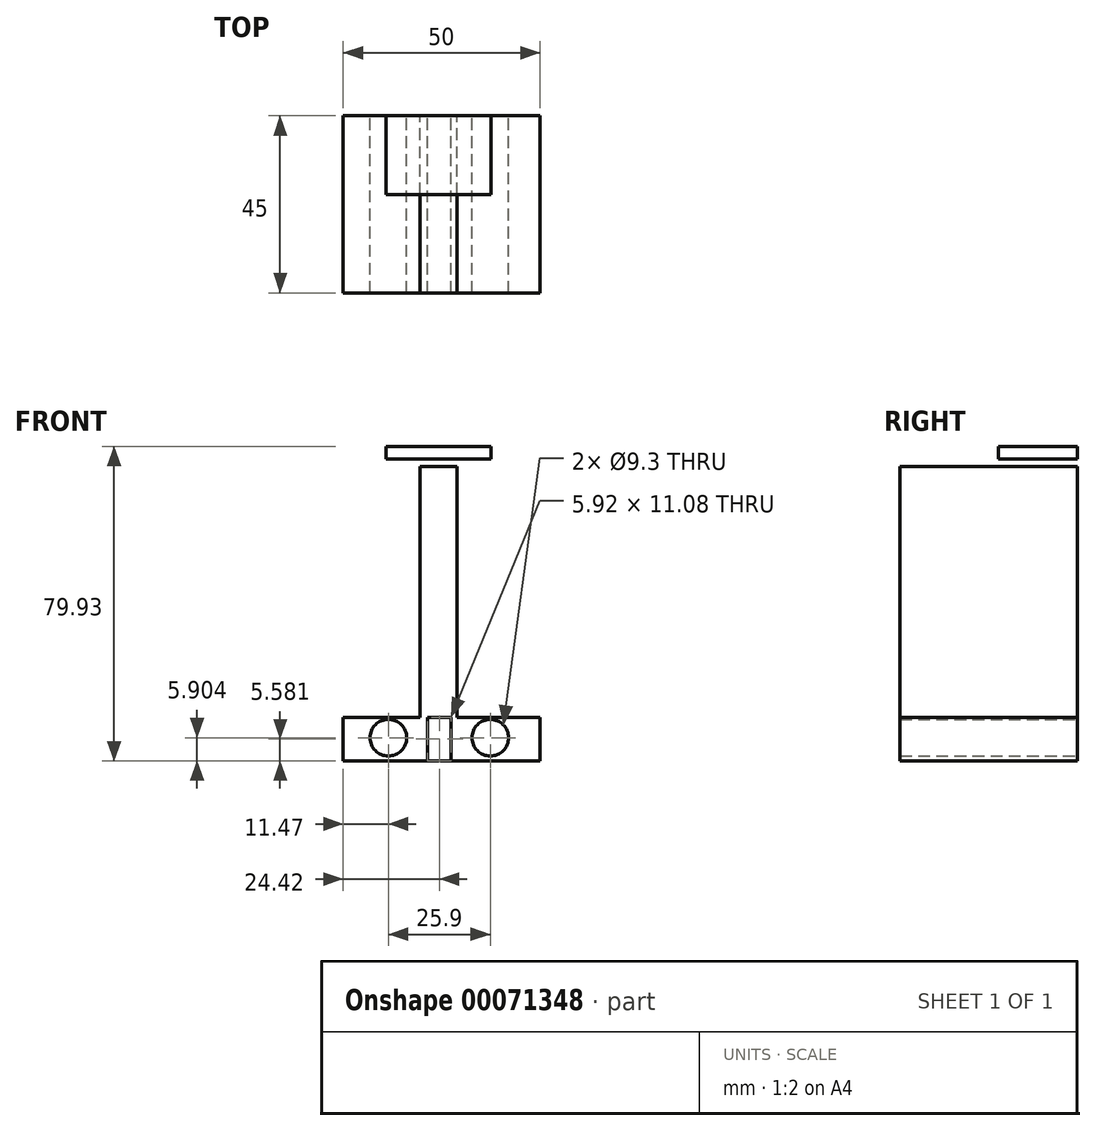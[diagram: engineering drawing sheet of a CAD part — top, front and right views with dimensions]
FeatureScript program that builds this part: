
annotation { "Feature Type Name" : "Feature", "Feature Type Description" : "" }
export const myFeature = defineFeature(function(context is Context, id is Id, definition is map)
    precondition{}
    {
        {
            var Q0;
            Q0=qCreatedBy(makeId("Front.planeOp"),FACE);
            var sketch = newSketch(context, id + "F0", { "sketchPlane" : qUnion([Q0])});
            skLineSegment(sketch, "E0.bottom", {"start": v(-4.86, 63.71) * mm, "end": v(4.48, 63.71) * mm});
            skLineSegment(sketch, "E0.top", {"start": v(-4.86, -11.08) * mm, "end": v(4.48, -11.08) * mm});
            skLineSegment(sketch, "E0.left", {"start": v(-4.86, 63.71) * mm, "end": v(-4.86, -11.08) * mm});
            skLineSegment(sketch, "E0.right", {"start": v(4.48, 63.71) * mm, "end": v(4.48, -11.08) * mm});
            skLineSegment(sketch, "E1.bottom", {"start": v(-24.42, 0) * mm, "end": v(25.58, 0) * mm});
            skLineSegment(sketch, "E1.top", {"start": v(-24.42, -11.12) * mm, "end": v(25.58, -11.12) * mm});
            skLineSegment(sketch, "E1.left", {"start": v(-24.42, 0) * mm, "end": v(-24.42, -11.12) * mm});
            skLineSegment(sketch, "E1.right", {"start": v(25.58, 0) * mm, "end": v(25.58, -11.12) * mm});
            skCircle(sketch, "E2", {"center": v(-12.95, -5.22) * mm, "radius": 4.65 * mm});
            skCircle(sketch, "E3.MirrorC", {"center": v(12.95, -5.22) * mm, "radius": 4.65 * mm});
            skLineSegment(sketch, "E4", {"start": v(-2.96, -11.08) * mm, "end": v(-2.96, 63.71) * mm});
            skLineSegment(sketch, "E5", {"start": v(-2.96, 63.71) * mm, "end": v(2.36, 63.71) * mm});
            skLineSegment(sketch, "E6.MirrorCS", {"start": v(2.96, -11.08) * mm, "end": v(2.96, 63.71) * mm});
            skLineSegment(sketch, "E7", {"start": v(-4.86, 63.71) * mm, "end": v(-6.73, 65.65) * mm});
            skLineSegment(sketch, "E8.MirrorCS", {"start": v(4.86, 63.71) * mm, "end": v(6.73, 65.65) * mm});
            skLineSegment(sketch, "E9.bottom", {"start": v(-13.5, 68.8) * mm, "end": v(13.12, 68.8) * mm});
            skLineSegment(sketch, "E9.top", {"start": v(-13.5, 65.63) * mm, "end": v(13.12, 65.63) * mm});
            skLineSegment(sketch, "E9.left", {"start": v(-13.5, 68.8) * mm, "end": v(-13.5, 65.63) * mm});
            skLineSegment(sketch, "E9.right", {"start": v(13.12, 68.8) * mm, "end": v(13.12, 65.63) * mm});
            skLineSegment(sketch, "E10", {"start": v(-6.73, 65.65) * mm, "end": v(-6.73, 68.8) * mm});
            skLineSegment(sketch, "E11", {"start": v(-6.73, 68.8) * mm, "end": v(6.73, 68.8) * mm});
            skLineSegment(sketch, "E12", {"start": v(6.73, 65.65) * mm, "end": v(6.73, 68.8) * mm});
            skLineSegment(sketch, "E13.bottom", {"start": v(-1.58, 63.71) * mm, "end": v(1.53, 63.71) * mm});
            skLineSegment(sketch, "E13.top", {"start": v(-1.58, 58.75) * mm, "end": v(1.53, 58.75) * mm});
            skLineSegment(sketch, "E13.left", {"start": v(-1.58, 63.71) * mm, "end": v(-1.58, 58.75) * mm});
            skLineSegment(sketch, "E13.right", {"start": v(1.53, 63.71) * mm, "end": v(1.53, 58.75) * mm});
            skSolve(sketch);
        }
        {
            var Q0;
            Q0 = qSketchRegion(id + "F0", true);
            extrude(context, id + "F1", {"entities" : qUnion([Q0]), "depth" : 20 * mm});
        }
        {
            var Q0;
            Q0=makeQuery(id+"F1.opExtrude","CAP_FACE",FACE,{"disambiguationData":[OSD([sQuery(id+"F0.wireOp",EDGE,"E0.bottom"),sQuery(id+"F0.wireOp",EDGE,"E0.top"),sQuery(id+"F0.wireOp",EDGE,"E0.left"),sQuery(id+"F0.wireOp",EDGE,"E0.right"),sQuery(id+"F0.wireOp",EDGE,"E1.bottom"),sQuery(id+"F0.wireOp",EDGE,"E1.top"),sQuery(id+"F0.wireOp",EDGE,"E1.left"),sQuery(id+"F0.wireOp",EDGE,"E1.right"),sQuery(id+"F0.wireOp",EDGE,"E2"),sQuery(id+"F0.wireOp",EDGE,"E3.MirrorC"),sQuery(id+"F0.wireOp",EDGE,"E4"),sQuery(id+"F0.wireOp",EDGE,"E5"),sQuery(id+"F0.wireOp",EDGE,"E6.MirrorCS"),sQuery(id+"F0.wireOp",EDGE,"E13.bottom")])],"isStart":false});
            extrude(context, id + "F2", {"entities" : qUnion([Q0]), "operationType" : NewBodyOperationType.ADD, "depth" : 25 * mm});
        }
    });
